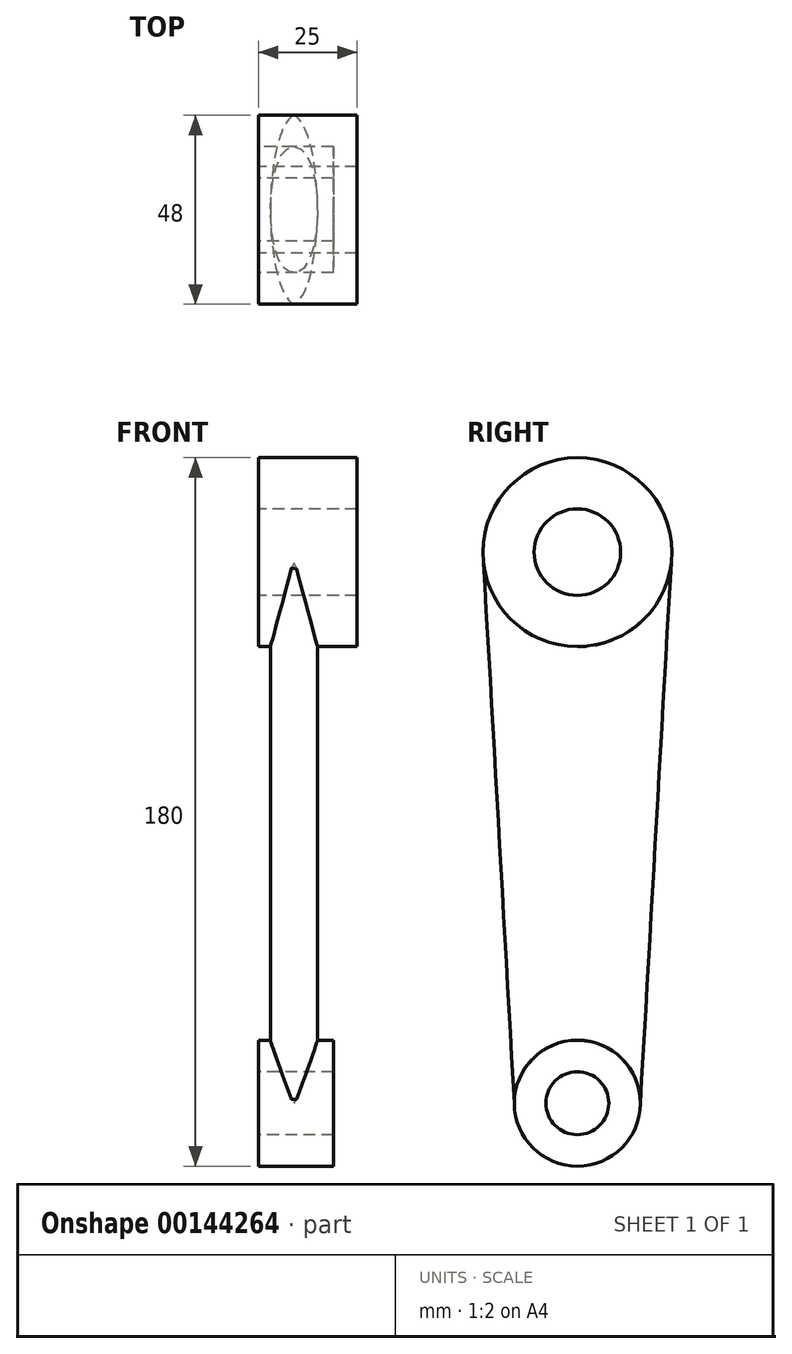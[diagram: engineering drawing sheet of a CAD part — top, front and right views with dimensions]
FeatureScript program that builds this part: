
annotation { "Feature Type Name" : "Feature", "Feature Type Description" : "" }
export const myFeature = defineFeature(function(context is Context, id is Id, definition is map)
    precondition{}
    {
        {
            var Q0;
            Q0=qCreatedBy(makeId("Right.planeOp"),FACE);
            var sketch = newSketch(context, id + "F0", { "sketchPlane" : qUnion([Q0])});
            skCircle(sketch, "E0", {"center": v(0, 0) * mm, "radius": 16 * mm});
            skCircle(sketch, "E1", {"center": v(0, 0) * mm, "radius": 8 * mm});
            skCircle(sketch, "E2", {"center": v(0, 140) * mm, "radius": 11 * mm});
            skCircle(sketch, "E3", {"center": v(0, 140) * mm, "radius": 24 * mm});
            skSolve(sketch);
        }
        {
            var Q0;
            Q0=makeQuery(id+"F0.imprint","IMPRINT",FACE,{"disambiguationData":[TD([[makeQuery(id+"F0.imprint","IMPRINT",EDGE,{"derivedFrom":sQuery(id+"F0.wireOp",EDGE,"E1")}),1.0]])]});
            var Q1;
            Q1=makeQuery(id+"F0.imprint","IMPRINT",FACE,{"disambiguationData":[TD([[makeQuery(id+"F0.imprint","IMPRINT",EDGE,{"derivedFrom":sQuery(id+"F0.wireOp",EDGE,"E0")}),1.0]])]});
            extrude(context, id + "F1", {"entities" : qUnion([Q0, Q1]), "depth" : 19 * mm});
        }
        {
            var Q0;
            Q0=makeQuery(id+"F0.imprint","IMPRINT",FACE,{"disambiguationData":[TD([[makeQuery(id+"F0.imprint","IMPRINT",EDGE,{"derivedFrom":sQuery(id+"F0.wireOp",EDGE,"E2")}),-1.0]])]});
            var Q1;
            Q1=makeQuery(id+"F0.imprint","IMPRINT",FACE,{"disambiguationData":[TD([[makeQuery(id+"F0.imprint","IMPRINT",EDGE,{"derivedFrom":sQuery(id+"F0.wireOp",EDGE,"E2")}),1.0]])]});
            extrude(context, id + "F2", {"entities" : qUnion([Q0, Q1]), "depth" : 25 * mm});
        }
        {
            var Q0;
            Q0=qCreatedBy(makeId("Top.planeOp"),FACE);
            var sketch = newSketch(context, id + "F3", { "sketchPlane" : qUnion([Q0])});
            skEllipse(sketch, "E4", {"center": v(9, 0) * mm, "majorRadius": 16 * mm, "minorRadius": 6 * mm, "majorAxis": v(0, 1)});
            skPoint(sketch, "E5", {"position": v(3, 0) * mm});
            skLineSegment(sketch, "E6", {"start": v(0, 16) * mm, "end": v(19, 16) * mm, "construction": true});
            skSolve(sketch);
        }
        {
            var Q0;
            Q0=sQuery(id+"F0.wireOp",VERTEX,"E3.center");
            var Q1;
            Q1=qCreatedBy(makeId("Top.planeOp"),FACE);
            cPlane(context, id + "F4", {"entities" : qUnion([Q0, Q1]), "cplaneType" : CPlaneType.PLANE_POINT, "offset" : 25 * mm, "width" : 150 * mm, "height" : 150 * mm});
        }
        {
            var Q0;
            Q0=qCreatedBy(id+"F4.planeOp",FACE);
            var sketch = newSketch(context, id + "F5", { "sketchPlane" : qUnion([Q0])});
            skEllipse(sketch, "E7", {"center": v(9, 0) * mm, "majorRadius": 24 * mm, "minorRadius": 6 * mm, "majorAxis": v(0, 1)});
            skPoint(sketch, "E8", {"position": v(3, 0) * mm});
            skLineSegment(sketch, "E9", {"start": v(0, 24) * mm, "end": v(25, 24) * mm, "construction": true});
            skSolve(sketch);
        }
        {
            var Q0;
            Q0=makeQuery(id+"F5.imprint","IMPRINT",FACE,{"disambiguationData":[TD([[makeQuery(id+"F5.imprint","IMPRINT",EDGE,{"derivedFrom":sQuery(id+"F5.wireOp",EDGE,"E7")}),1.0]])]});
            var Q1;
            Q1=makeQuery(id+"F3.imprint","IMPRINT",FACE,{"disambiguationData":[TD([[makeQuery(id+"F3.imprint","IMPRINT",EDGE,{"derivedFrom":sQuery(id+"F3.wireOp",EDGE,"E4")}),1.0]])]});
            loft(context, id + "F6", {"operationType" : NewBodyOperationType.ADD, "sheetProfilesArray" : [{ "sheetProfileEntities" : qUnion([Q0]) }, { "sheetProfileEntities" : qUnion([Q1]) }]});
        }
        {
            var Q0;
            Q0=makeQuery(id+"F0.imprint","IMPRINT",FACE,{"disambiguationData":[TD([[makeQuery(id+"F0.imprint","IMPRINT",EDGE,{"derivedFrom":sQuery(id+"F0.wireOp",EDGE,"E2")}),1.0]])]});
            extrude(context, id + "F7", {"entities" : qUnion([Q0]), "operationType" : NewBodyOperationType.REMOVE, "endBound" : BoundingType.THROUGH_ALL, "depth" : 25 * mm});
        }
        {
            var Q0;
            Q0=makeQuery(id+"F0.imprint","IMPRINT",FACE,{"disambiguationData":[TD([[makeQuery(id+"F0.imprint","IMPRINT",EDGE,{"derivedFrom":sQuery(id+"F0.wireOp",EDGE,"E1")}),1.0]])]});
            extrude(context, id + "F8", {"entities" : qUnion([Q0]), "operationType" : NewBodyOperationType.REMOVE, "endBound" : BoundingType.THROUGH_ALL, "depth" : 25 * mm});
        }
    });
